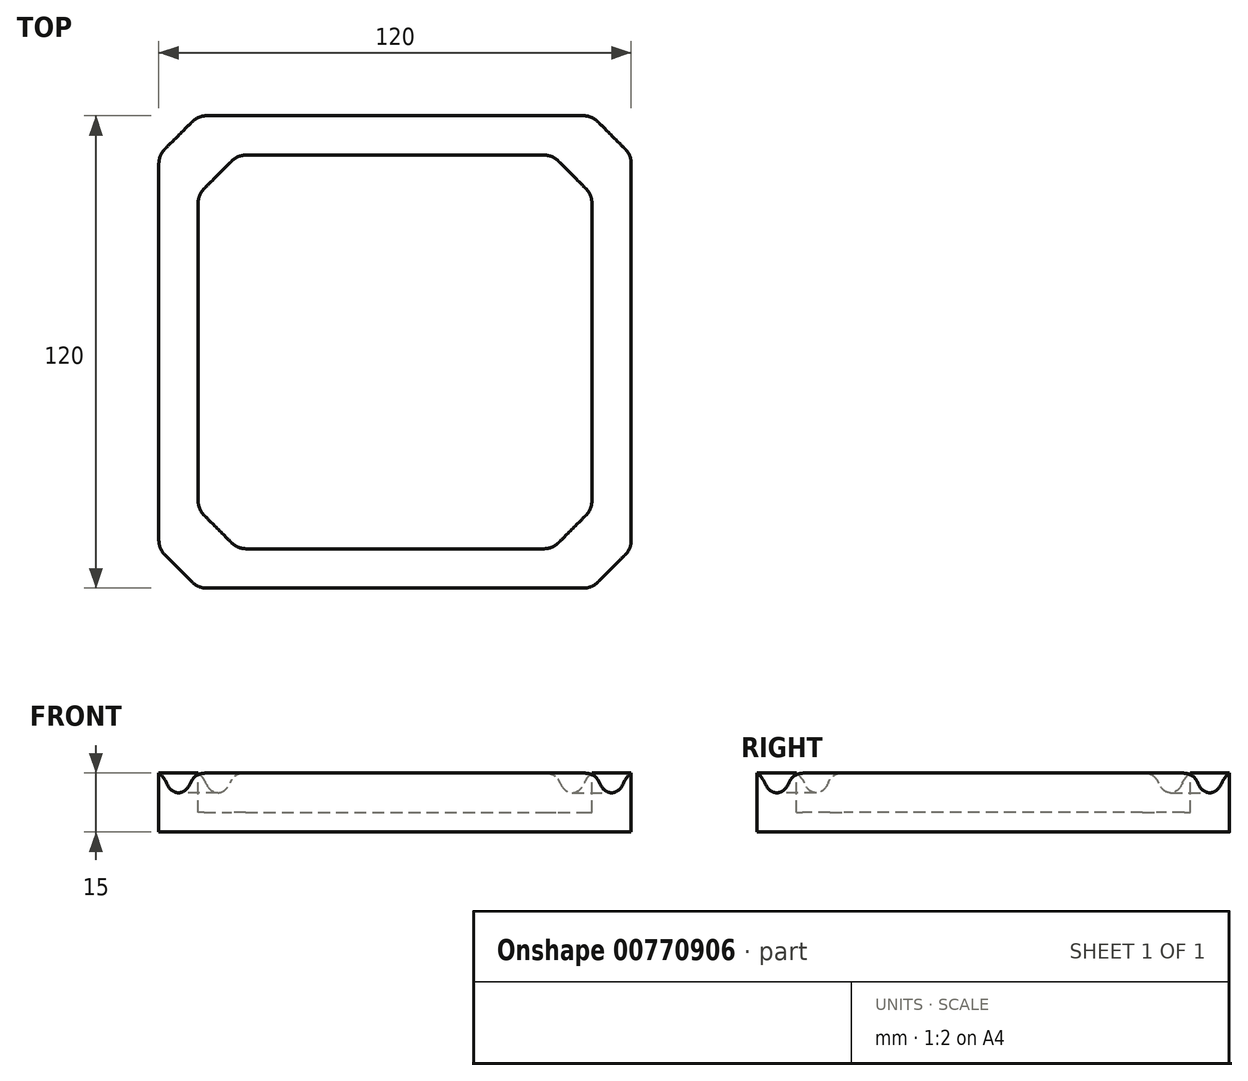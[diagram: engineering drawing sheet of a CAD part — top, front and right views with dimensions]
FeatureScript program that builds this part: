
annotation { "Feature Type Name" : "Feature", "Feature Type Description" : "" }
export const myFeature = defineFeature(function(context is Context, id is Id, definition is map)
    precondition{}
    {
        {
            var Q0;
            Q0=qCreatedBy(makeId("Top.planeOp"),FACE);
            var sketch = newSketch(context, id + "F0", { "sketchPlane" : qUnion([Q0])});
            skLineSegment(sketch, "E0.bottom", {"start": v(-50, 60) * mm, "end": v(50, 60) * mm});
            skLineSegment(sketch, "E0.top", {"start": v(-50, -60) * mm, "end": v(50, -60) * mm});
            skLineSegment(sketch, "E0.left", {"start": v(-60, 50) * mm, "end": v(-60, -50) * mm});
            skLineSegment(sketch, "E0.right", {"start": v(60, 50) * mm, "end": v(60, -50) * mm});
            skLineSegment(sketch, "E1", {"start": v(-60, 50) * mm, "end": v(-50, 60) * mm});
            skLineSegment(sketch, "E2", {"start": v(50, 60) * mm, "end": v(60, 50) * mm});
            skLineSegment(sketch, "E3", {"start": v(60, -50) * mm, "end": v(50, -60) * mm});
            skLineSegment(sketch, "E4", {"start": v(-60, -50) * mm, "end": v(-50, -60) * mm});
            skSolve(sketch);
        }
        {
            var Q0;
            Q0=makeQuery(id+"F0.imprint","IMPRINT",FACE,{"disambiguationData":[TD([[makeQuery(id+"F0.imprint","IMPRINT",EDGE,{"derivedFrom":sQuery(id+"F0.wireOp",EDGE,"E0.bottom")}),-1.0]])]});
            extrude(context, id + "F1", {"entities" : qUnion([Q0]), "depth" : 15 * mm, "offsetDistance" : 25 * mm});
        }
        {
            var Q0;
            Q0=makeQuery(id+"F1.opExtrude","CAP_FACE",FACE,{"disambiguationData":[OSD([sQuery(id+"F0.wireOp",EDGE,"E0.bottom"),sQuery(id+"F0.wireOp",EDGE,"E0.top"),sQuery(id+"F0.wireOp",EDGE,"E0.left"),sQuery(id+"F0.wireOp",EDGE,"E0.right"),sQuery(id+"F0.wireOp",EDGE,"E1"),sQuery(id+"F0.wireOp",EDGE,"E2"),sQuery(id+"F0.wireOp",EDGE,"E3"),sQuery(id+"F0.wireOp",EDGE,"E4")])],"isStart":false});
            var sketch = newSketch(context, id + "F2", { "sketchPlane" : qUnion([Q0])});
            skLineSegment(sketch, "E5.bottom", {"start": v(-40, 50) * mm, "end": v(40, 50) * mm});
            skLineSegment(sketch, "E5.top", {"start": v(-40, -50) * mm, "end": v(40, -50) * mm});
            skLineSegment(sketch, "E5.left", {"start": v(-50, 40) * mm, "end": v(-50, -40) * mm});
            skLineSegment(sketch, "E5.right", {"start": v(50, 40) * mm, "end": v(50, -40) * mm});
            skLineSegment(sketch, "E6", {"start": v(-50, 40) * mm, "end": v(-40, 50) * mm});
            skLineSegment(sketch, "E7", {"start": v(40, 50) * mm, "end": v(50, 40) * mm});
            skLineSegment(sketch, "E8", {"start": v(50, -40) * mm, "end": v(40, -50) * mm});
            skLineSegment(sketch, "E9", {"start": v(-50, -40) * mm, "end": v(-40, -50) * mm});
            skSolve(sketch);
        }
        {
            var Q0;
            Q0=makeQuery(id+"F2.imprint","IMPRINT",FACE,{"disambiguationData":[TD([[makeQuery(id+"F2.imprint","IMPRINT",EDGE,{"derivedFrom":sQuery(id+"F2.wireOp",EDGE,"E5.bottom")}),-1.0]])]});
            extrude(context, id + "F3", {"entities" : qUnion([Q0]), "operationType" : NewBodyOperationType.REMOVE, "oppositeDirection" : true, "depth" : 10 * mm, "offsetDistance" : 25 * mm});
        }
        {
            var Q0;
            Q0=makeQuery(id+"F1.opExtrude","SWEPT_FACE",FACE,{"disambiguationData":[OSD([sQuery(id+"F0.wireOp",EDGE,"E1")])]});
            cPlane(context, id + "F4", {"entities" : qUnion([Q0]), "cplaneType" : CPlaneType.OFFSET, "offset" : .1 * mm, "width" : 150 * mm, "height" : 150 * mm});
        }
        {
            var Q0;
            Q0=qCreatedBy(id+"F4.planeOp",FACE);
            var sketch = newSketch(context, id + "F5", { "sketchPlane" : qUnion([Q0])});
            skCircle(sketch, "E10", {"center": v(0, 15) * mm, "radius": 5 * mm});
            skSolve(sketch);
        }
        {
            var Q0;
            Q0=makeQuery(id+"F5.imprint","IMPRINT",FACE,{"disambiguationData":[TD([[makeQuery(id+"F5.imprint","IMPRINT",EDGE,{"derivedFrom":sQuery(id+"F5.wireOp",EDGE,"E10")}),1.0]])]});
            extrude(context, id + "F6", {"entities" : qUnion([Q0]), "operationType" : NewBodyOperationType.REMOVE, "oppositeDirection" : true, "depth" : 15 * mm, "offsetDistance" : 25 * mm});
        }
        {
            var Q0;
            Q0=makeQuery(id+"F1.opExtrude","SWEPT_FACE",FACE,{"disambiguationData":[OSD([sQuery(id+"F0.wireOp",EDGE,"E2")])]});
            cPlane(context, id + "F7", {"entities" : qUnion([Q0]), "cplaneType" : CPlaneType.OFFSET, "offset" : .1 * mm, "width" : 150 * mm, "height" : 150 * mm});
        }
        {
            var Q0;
            Q0=qCreatedBy(id+"F7.planeOp",FACE);
            var sketch = newSketch(context, id + "F8", { "sketchPlane" : qUnion([Q0])});
            skCircle(sketch, "E11", {"center": v(0, 15) * mm, "radius": 5 * mm});
            skSolve(sketch);
        }
        {
            var Q0;
            Q0=makeQuery(id+"F8.imprint","IMPRINT",FACE,{"disambiguationData":[TD([[makeQuery(id+"F8.imprint","IMPRINT",EDGE,{"derivedFrom":sQuery(id+"F8.wireOp",EDGE,"E11")}),1.0]])]});
            extrude(context, id + "F9", {"entities" : qUnion([Q0]), "operationType" : NewBodyOperationType.REMOVE, "oppositeDirection" : true, "depth" : 15 * mm, "offsetDistance" : 25 * mm});
        }
        {
            var Q0;
            Q0=makeQuery(id+"F1.opExtrude","SWEPT_FACE",FACE,{"disambiguationData":[OSD([sQuery(id+"F0.wireOp",EDGE,"E3")])]});
            cPlane(context, id + "F10", {"entities" : qUnion([Q0]), "cplaneType" : CPlaneType.OFFSET, "offset" : .1 * mm, "width" : 150 * mm, "height" : 150 * mm});
        }
        {
            var Q0;
            Q0=qCreatedBy(id+"F10.planeOp",FACE);
            var sketch = newSketch(context, id + "F11", { "sketchPlane" : qUnion([Q0])});
            skCircle(sketch, "E12", {"center": v(0, 15) * mm, "radius": 5 * mm});
            skSolve(sketch);
        }
        {
            var Q0;
            Q0=makeQuery(id+"F11.imprint","IMPRINT",FACE,{"disambiguationData":[TD([[makeQuery(id+"F11.imprint","IMPRINT",EDGE,{"derivedFrom":sQuery(id+"F11.wireOp",EDGE,"E12")}),1.0]])]});
            extrude(context, id + "F12", {"entities" : qUnion([Q0]), "operationType" : NewBodyOperationType.REMOVE, "oppositeDirection" : true, "depth" : 15 * mm, "offsetDistance" : 25 * mm});
        }
        {
            var Q0;
            Q0=makeQuery(id+"F1.opExtrude","SWEPT_FACE",FACE,{"disambiguationData":[OSD([sQuery(id+"F0.wireOp",EDGE,"E4")])]});
            cPlane(context, id + "F13", {"entities" : qUnion([Q0]), "cplaneType" : CPlaneType.OFFSET, "offset" : .1 * mm, "width" : 150 * mm, "height" : 150 * mm});
        }
        {
            var Q0;
            Q0=qCreatedBy(id+"F13.planeOp",FACE);
            var sketch = newSketch(context, id + "F14", { "sketchPlane" : qUnion([Q0])});
            skCircle(sketch, "E13", {"center": v(0, 15) * mm, "radius": 5 * mm});
            skSolve(sketch);
        }
        {
            var Q0;
            Q0=makeQuery(id+"F14.imprint","IMPRINT",FACE,{"disambiguationData":[TD([[makeQuery(id+"F14.imprint","IMPRINT",EDGE,{"derivedFrom":sQuery(id+"F14.wireOp",EDGE,"E13")}),1.0]])]});
            extrude(context, id + "F15", {"entities" : qUnion([Q0]), "operationType" : NewBodyOperationType.REMOVE, "oppositeDirection" : true, "depth" : 15 * mm, "offsetDistance" : 25 * mm});
        }
        {
            var Q0;
            Q0=makeQuery(id+"F6.boolean.opBoolean","INTERSECT",EDGE,{"disambiguationData":[OD(1.0)],"derivedFrom":[makeQuery(id+"F1.opExtrude","CAP_FACE",FACE,{"disambiguationData":[OSD([sQuery(id+"F0.wireOp",EDGE,"E0.bottom"),sQuery(id+"F0.wireOp",EDGE,"E0.top"),sQuery(id+"F0.wireOp",EDGE,"E0.left"),sQuery(id+"F0.wireOp",EDGE,"E0.right"),sQuery(id+"F0.wireOp",EDGE,"E1"),sQuery(id+"F0.wireOp",EDGE,"E2"),sQuery(id+"F0.wireOp",EDGE,"E3"),sQuery(id+"F0.wireOp",EDGE,"E4")])],"isStart":false}),makeQuery(id+"F6.opExtrude","SWEPT_FACE",FACE,{"disambiguationData":[OSD([sQuery(id+"F5.wireOp",EDGE,"E10")])]})]});
            var Q1;
            Q1=makeQuery(id+"F6.boolean.opBoolean","INTERSECT",EDGE,{"disambiguationData":[OD(0.0)],"derivedFrom":[makeQuery(id+"F1.opExtrude","CAP_FACE",FACE,{"disambiguationData":[OSD([sQuery(id+"F0.wireOp",EDGE,"E0.bottom"),sQuery(id+"F0.wireOp",EDGE,"E0.top"),sQuery(id+"F0.wireOp",EDGE,"E0.left"),sQuery(id+"F0.wireOp",EDGE,"E0.right"),sQuery(id+"F0.wireOp",EDGE,"E1"),sQuery(id+"F0.wireOp",EDGE,"E2"),sQuery(id+"F0.wireOp",EDGE,"E3"),sQuery(id+"F0.wireOp",EDGE,"E4")])],"isStart":false}),makeQuery(id+"F6.opExtrude","SWEPT_FACE",FACE,{"disambiguationData":[OSD([sQuery(id+"F5.wireOp",EDGE,"E10")])]})]});
            var Q2;
            {var subQ5=sQuery(id+"F0.wireOp",EDGE,"E4");var subQ7=sQuery(id+"F0.wireOp",EDGE,"E0.top");var subQ8=makeQuery(id+"F1.opExtrude","SWEPT_FACE",FACE,{"disambiguationData":[OSD([subQ7])]});var subQ10=sQuery(id+"F0.wireOp",EDGE,"E3");var subQ12=sQuery(id+"F0.wireOp",EDGE,"E0.left");var subQ14=sQuery(id+"F0.wireOp",EDGE,"E1");var subQ16=sQuery(id+"F0.wireOp",EDGE,"E2");var subQ17=sQuery(id+"F0.wireOp",EDGE,"E0.right");Q2=makeQuery(id+"F15.boolean.opBoolean","INTERSECT",EDGE,{"disambiguationData":[OD(1.0)],"derivedFrom":[makeQuery(id+"F12.boolean.opBoolean","SPLIT",FACE,{"disambiguationData":[TD([subQ8])],"derivedFrom":makeQuery(id+"F9.boolean.opBoolean","SPLIT",FACE,{"disambiguationData":[TD([subQ8])],"derivedFrom":makeQuery(id+"F1.opExtrude","CAP_FACE",FACE,{"disambiguationData":[OSD([sQuery(id+"F0.wireOp",EDGE,"E0.bottom"),subQ7,subQ12,subQ17,subQ14,subQ16,subQ10,subQ5])],"isStart":false})})}),makeQuery(id+"F15.opExtrude","SWEPT_FACE",FACE,{"disambiguationData":[OSD([sQuery(id+"F14.wireOp",EDGE,"E13")])]})]});}
            var Q3;
            {var subQ5=sQuery(id+"F0.wireOp",EDGE,"E4");var subQ7=sQuery(id+"F0.wireOp",EDGE,"E0.top");var subQ8=makeQuery(id+"F1.opExtrude","SWEPT_FACE",FACE,{"disambiguationData":[OSD([subQ7])]});var subQ10=sQuery(id+"F0.wireOp",EDGE,"E3");var subQ12=sQuery(id+"F0.wireOp",EDGE,"E0.left");var subQ14=sQuery(id+"F0.wireOp",EDGE,"E1");var subQ16=sQuery(id+"F0.wireOp",EDGE,"E2");var subQ17=sQuery(id+"F0.wireOp",EDGE,"E0.right");Q3=makeQuery(id+"F15.boolean.opBoolean","INTERSECT",EDGE,{"disambiguationData":[OD(0.0)],"derivedFrom":[makeQuery(id+"F12.boolean.opBoolean","SPLIT",FACE,{"disambiguationData":[TD([subQ8])],"derivedFrom":makeQuery(id+"F9.boolean.opBoolean","SPLIT",FACE,{"disambiguationData":[TD([subQ8])],"derivedFrom":makeQuery(id+"F1.opExtrude","CAP_FACE",FACE,{"disambiguationData":[OSD([sQuery(id+"F0.wireOp",EDGE,"E0.bottom"),subQ7,subQ12,subQ17,subQ14,subQ16,subQ10,subQ5])],"isStart":false})})}),makeQuery(id+"F15.opExtrude","SWEPT_FACE",FACE,{"disambiguationData":[OSD([sQuery(id+"F14.wireOp",EDGE,"E13")])]})]});}
            var Q4;
            {var subQ0=sQuery(id+"F0.wireOp",EDGE,"E4");var subQ1=sQuery(id+"F0.wireOp",EDGE,"E3");var subQ2=sQuery(id+"F0.wireOp",EDGE,"E2");var subQ3=sQuery(id+"F0.wireOp",EDGE,"E0.top");var subQ4=sQuery(id+"F0.wireOp",EDGE,"E0.left");var subQ5=sQuery(id+"F0.wireOp",EDGE,"E0.right");var subQ6=sQuery(id+"F0.wireOp",EDGE,"E1");Q4=makeQuery(id+"F12.boolean.opBoolean","INTERSECT",EDGE,{"disambiguationData":[OD(0.0)],"derivedFrom":[makeQuery(id+"F9.boolean.opBoolean","SPLIT",FACE,{"disambiguationData":[TD([makeQuery(id+"F1.opExtrude","SWEPT_FACE",FACE,{"disambiguationData":[OSD([subQ3])]})])],"derivedFrom":makeQuery(id+"F1.opExtrude","CAP_FACE",FACE,{"disambiguationData":[OSD([sQuery(id+"F0.wireOp",EDGE,"E0.bottom"),subQ3,subQ4,subQ5,subQ6,subQ2,subQ1,subQ0])],"isStart":false})}),makeQuery(id+"F12.opExtrude","SWEPT_FACE",FACE,{"disambiguationData":[OSD([sQuery(id+"F11.wireOp",EDGE,"E12")])]})]});}
            var Q5;
            {var subQ0=sQuery(id+"F0.wireOp",EDGE,"E4");var subQ1=sQuery(id+"F0.wireOp",EDGE,"E3");var subQ2=sQuery(id+"F0.wireOp",EDGE,"E2");var subQ3=sQuery(id+"F0.wireOp",EDGE,"E0.top");var subQ4=sQuery(id+"F0.wireOp",EDGE,"E0.left");var subQ5=sQuery(id+"F0.wireOp",EDGE,"E0.right");var subQ6=sQuery(id+"F0.wireOp",EDGE,"E1");Q5=makeQuery(id+"F12.boolean.opBoolean","INTERSECT",EDGE,{"disambiguationData":[OD(1.0)],"derivedFrom":[makeQuery(id+"F9.boolean.opBoolean","SPLIT",FACE,{"disambiguationData":[TD([makeQuery(id+"F1.opExtrude","SWEPT_FACE",FACE,{"disambiguationData":[OSD([subQ3])]})])],"derivedFrom":makeQuery(id+"F1.opExtrude","CAP_FACE",FACE,{"disambiguationData":[OSD([sQuery(id+"F0.wireOp",EDGE,"E0.bottom"),subQ3,subQ4,subQ5,subQ6,subQ2,subQ1,subQ0])],"isStart":false})}),makeQuery(id+"F12.opExtrude","SWEPT_FACE",FACE,{"disambiguationData":[OSD([sQuery(id+"F11.wireOp",EDGE,"E12")])]})]});}
            var Q6;
            Q6=makeQuery(id+"F9.boolean.opBoolean","INTERSECT",EDGE,{"disambiguationData":[OD(1.0)],"derivedFrom":[makeQuery(id+"F1.opExtrude","CAP_FACE",FACE,{"disambiguationData":[OSD([sQuery(id+"F0.wireOp",EDGE,"E0.bottom"),sQuery(id+"F0.wireOp",EDGE,"E0.top"),sQuery(id+"F0.wireOp",EDGE,"E0.left"),sQuery(id+"F0.wireOp",EDGE,"E0.right"),sQuery(id+"F0.wireOp",EDGE,"E1"),sQuery(id+"F0.wireOp",EDGE,"E2"),sQuery(id+"F0.wireOp",EDGE,"E3"),sQuery(id+"F0.wireOp",EDGE,"E4")])],"isStart":false}),makeQuery(id+"F9.opExtrude","SWEPT_FACE",FACE,{"disambiguationData":[OSD([sQuery(id+"F8.wireOp",EDGE,"E11")])]})]});
            var Q7;
            Q7=makeQuery(id+"F9.boolean.opBoolean","INTERSECT",EDGE,{"disambiguationData":[OD(0.0)],"derivedFrom":[makeQuery(id+"F1.opExtrude","CAP_FACE",FACE,{"disambiguationData":[OSD([sQuery(id+"F0.wireOp",EDGE,"E0.bottom"),sQuery(id+"F0.wireOp",EDGE,"E0.top"),sQuery(id+"F0.wireOp",EDGE,"E0.left"),sQuery(id+"F0.wireOp",EDGE,"E0.right"),sQuery(id+"F0.wireOp",EDGE,"E1"),sQuery(id+"F0.wireOp",EDGE,"E2"),sQuery(id+"F0.wireOp",EDGE,"E3"),sQuery(id+"F0.wireOp",EDGE,"E4")])],"isStart":false}),makeQuery(id+"F9.opExtrude","SWEPT_FACE",FACE,{"disambiguationData":[OSD([sQuery(id+"F8.wireOp",EDGE,"E11")])]})]});
            fillet(context, id + "F16", {"entities" : qUnion([Q0, Q1, Q2, Q3, Q4, Q5, Q6, Q7]), "radius" : 5 * mm, "tangentPropagation" : true, "allowEdgeOverflow" : false});
        }
        {
            var Q0;
            Q0=makeQuery(id+"F1.opExtrude","SWEPT_EDGE",EDGE,{"disambiguationData":[OSD([sQuery(id+"F0.wireOp",EDGE,"E0.left"),sQuery(id+"F0.wireOp",EDGE,"E1")])]});
            var Q1;
            Q1=makeQuery(id+"F1.opExtrude","SWEPT_EDGE",EDGE,{"disambiguationData":[OSD([sQuery(id+"F0.wireOp",EDGE,"E0.bottom"),sQuery(id+"F0.wireOp",EDGE,"E1")])]});
            var Q2;
            Q2=makeQuery(id+"F1.opExtrude","SWEPT_EDGE",EDGE,{"disambiguationData":[OSD([sQuery(id+"F0.wireOp",EDGE,"E0.left"),sQuery(id+"F0.wireOp",EDGE,"E4")])]});
            var Q3;
            Q3=makeQuery(id+"F1.opExtrude","SWEPT_EDGE",EDGE,{"disambiguationData":[OSD([sQuery(id+"F0.wireOp",EDGE,"E0.top"),sQuery(id+"F0.wireOp",EDGE,"E4")])]});
            var Q4;
            Q4=makeQuery(id+"F1.opExtrude","SWEPT_EDGE",EDGE,{"disambiguationData":[OSD([sQuery(id+"F0.wireOp",EDGE,"E0.top"),sQuery(id+"F0.wireOp",EDGE,"E3")])]});
            var Q5;
            Q5=makeQuery(id+"F1.opExtrude","SWEPT_EDGE",EDGE,{"disambiguationData":[OSD([sQuery(id+"F0.wireOp",EDGE,"E0.right"),sQuery(id+"F0.wireOp",EDGE,"E3")])]});
            var Q6;
            Q6=makeQuery(id+"F1.opExtrude","SWEPT_EDGE",EDGE,{"disambiguationData":[OSD([sQuery(id+"F0.wireOp",EDGE,"E0.right"),sQuery(id+"F0.wireOp",EDGE,"E2")])]});
            var Q7;
            Q7=makeQuery(id+"F1.opExtrude","SWEPT_EDGE",EDGE,{"disambiguationData":[OSD([sQuery(id+"F0.wireOp",EDGE,"E0.bottom"),sQuery(id+"F0.wireOp",EDGE,"E2")])]});
            fillet(context, id + "F17", {"entities" : qUnion([Q0, Q1, Q2, Q3, Q4, Q5, Q6, Q7]), "radius" : 5 * mm, "tangentPropagation" : true, "allowEdgeOverflow" : false});
        }
        {
            var Q0;
            Q0=makeQuery(id+"F3.boolean.opBoolean","COPY",EDGE,{"derivedFrom":makeQuery(id+"F3.opExtrude","SWEPT_EDGE",EDGE,{"disambiguationData":[OSD([sQuery(id+"F2.wireOp",EDGE,"E5.top"),sQuery(id+"F2.wireOp",EDGE,"E9")])]})});
            var Q1;
            Q1=makeQuery(id+"F3.boolean.opBoolean","COPY",EDGE,{"derivedFrom":makeQuery(id+"F3.opExtrude","SWEPT_EDGE",EDGE,{"disambiguationData":[OSD([sQuery(id+"F2.wireOp",EDGE,"E5.left"),sQuery(id+"F2.wireOp",EDGE,"E9")])]})});
            var Q2;
            Q2=makeQuery(id+"F3.boolean.opBoolean","COPY",EDGE,{"derivedFrom":makeQuery(id+"F3.opExtrude","SWEPT_EDGE",EDGE,{"disambiguationData":[OSD([sQuery(id+"F2.wireOp",EDGE,"E5.left"),sQuery(id+"F2.wireOp",EDGE,"E6")])]})});
            var Q3;
            Q3=makeQuery(id+"F3.boolean.opBoolean","COPY",EDGE,{"derivedFrom":makeQuery(id+"F3.opExtrude","SWEPT_EDGE",EDGE,{"disambiguationData":[OSD([sQuery(id+"F2.wireOp",EDGE,"E5.bottom"),sQuery(id+"F2.wireOp",EDGE,"E6")])]})});
            var Q4;
            Q4=makeQuery(id+"F3.boolean.opBoolean","COPY",EDGE,{"derivedFrom":makeQuery(id+"F3.opExtrude","SWEPT_EDGE",EDGE,{"disambiguationData":[OSD([sQuery(id+"F2.wireOp",EDGE,"E5.bottom"),sQuery(id+"F2.wireOp",EDGE,"E7")])]})});
            var Q5;
            Q5=makeQuery(id+"F3.boolean.opBoolean","COPY",EDGE,{"derivedFrom":makeQuery(id+"F3.opExtrude","SWEPT_EDGE",EDGE,{"disambiguationData":[OSD([sQuery(id+"F2.wireOp",EDGE,"E5.right"),sQuery(id+"F2.wireOp",EDGE,"E7")])]})});
            var Q6;
            Q6=makeQuery(id+"F3.boolean.opBoolean","COPY",EDGE,{"derivedFrom":makeQuery(id+"F3.opExtrude","SWEPT_EDGE",EDGE,{"disambiguationData":[OSD([sQuery(id+"F2.wireOp",EDGE,"E5.right"),sQuery(id+"F2.wireOp",EDGE,"E8")])]})});
            var Q7;
            Q7=makeQuery(id+"F3.boolean.opBoolean","COPY",EDGE,{"derivedFrom":makeQuery(id+"F3.opExtrude","SWEPT_EDGE",EDGE,{"disambiguationData":[OSD([sQuery(id+"F2.wireOp",EDGE,"E5.top"),sQuery(id+"F2.wireOp",EDGE,"E8")])]})});
            fillet(context, id + "F18", {"entities" : qUnion([Q0, Q1, Q2, Q3, Q4, Q5, Q6, Q7]), "radius" : 5 * mm, "tangentPropagation" : true, "allowEdgeOverflow" : false});
        }
    });
